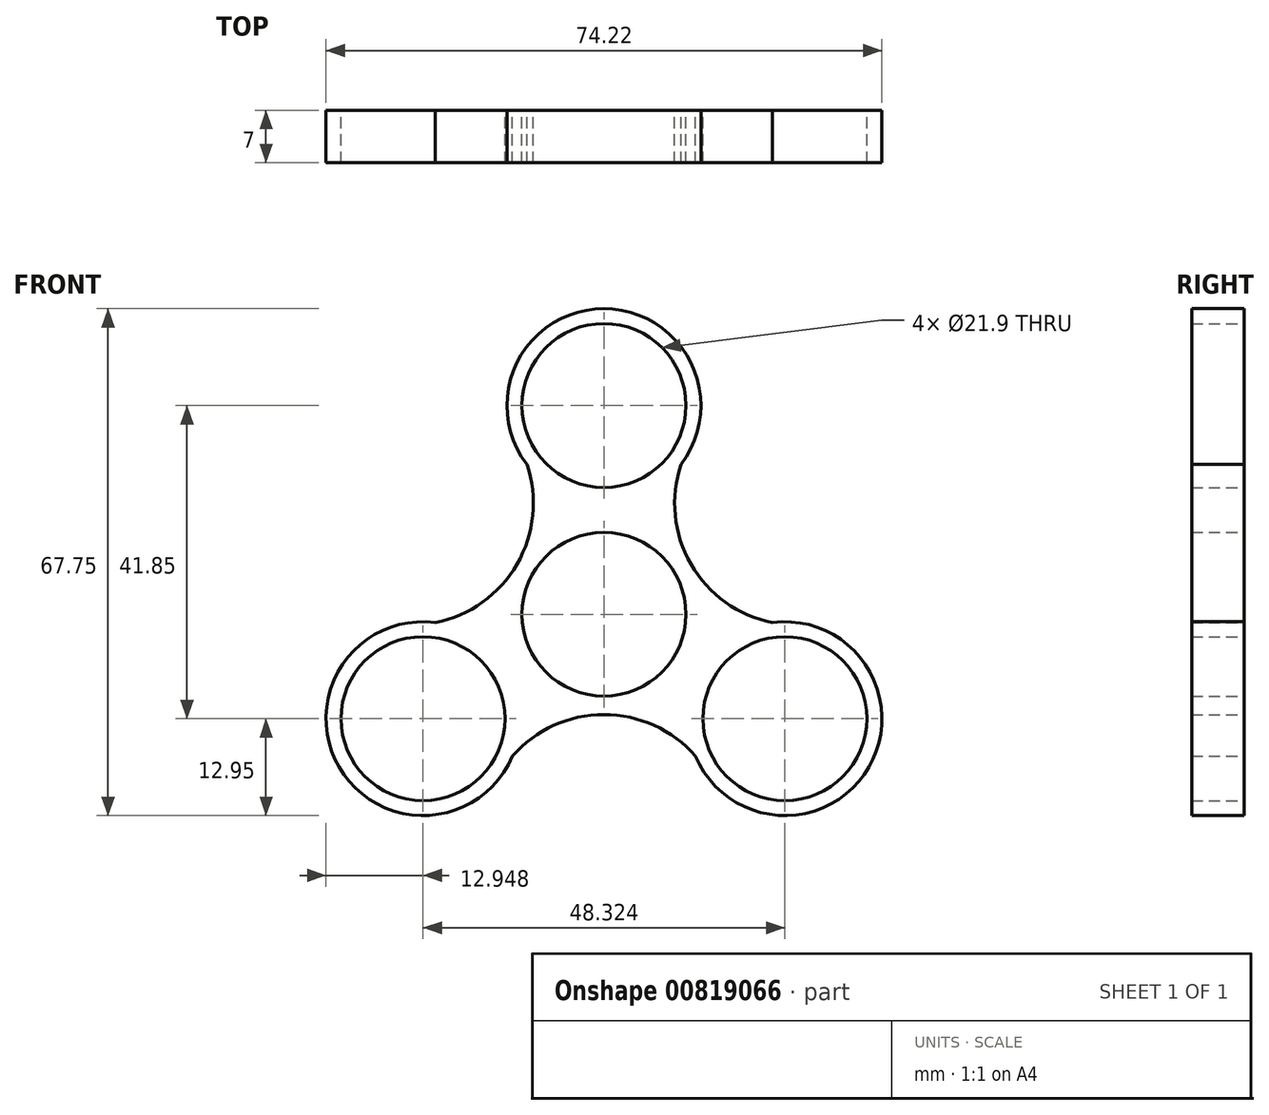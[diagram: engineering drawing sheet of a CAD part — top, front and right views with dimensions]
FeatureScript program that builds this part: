
annotation { "Feature Type Name" : "Feature", "Feature Type Description" : "" }
export const myFeature = defineFeature(function(context is Context, id is Id, definition is map)
    precondition{}
    {
        {
            var Q0;
            Q0=qCreatedBy(makeId("Front.planeOp"),FACE);
            var sketch = newSketch(context, id + "F0", { "sketchPlane" : qUnion([Q0])});
            skCircle(sketch, "E0", {"center": v(0, 0) * mm, "radius": 10.95 * mm});
            skCircle(sketch, "E1.0", {"center": v(0, 0) * mm, "radius": 12.95 * mm});
            skCircle(sketch, "E2", {"center": v(0, 27.9) * mm, "radius": 10.95 * mm});
            skCircle(sketch, "E3.0", {"center": v(0, 27.9) * mm, "radius": 12.95 * mm});
            skCircle(sketch, "E4.1.0", {"center": v(-24.16, -13.95) * mm, "radius": 12.95 * mm});
            skCircle(sketch, "E4.1.1", {"center": v(-24.16, -13.95) * mm, "radius": 10.95 * mm});
            skCircle(sketch, "E4.2.0", {"center": v(24.16, -13.95) * mm, "radius": 12.95 * mm});
            skCircle(sketch, "E4.2.1", {"center": v(24.16, -13.95) * mm, "radius": 10.95 * mm});
            skArc(sketch, "E5", {"start": v(10.3, 20.05) * mm, "mid": v(11.6, 6.7) * mm, "end": v(22.52, -1.1) * mm});
            skArc(sketch, "E6.1.0", {"start": v(-22.52, -1.1) * mm, "mid": v(-11.6, 6.7) * mm, "end": v(-10.3, 20.05) * mm});
            skArc(sketch, "E6.2.0", {"start": v(12.22, -18.95) * mm, "mid": v(0, -13.4) * mm, "end": v(-12.22, -18.95) * mm});
            skSolve(sketch);
        }
        {
            var Q0;
            Q0 = qSketchRegion(id + "F0", true);
            var Q1;
            Q1=makeQuery(id+"F0.imprint","IMPRINT",FACE,{"disambiguationData":[TD([[makeQuery(id+"F0.imprint","IMPRINT",EDGE,{"derivedFrom":sQuery(id+"F0.wireOp",EDGE,"E0")}),-1.0]])]});
            extrude(context, id + "F1", {"entities" : qUnion([Q0, Q1]), "depth" : 7 * mm, "offsetDistance" : 25 * mm});
        }
    });
